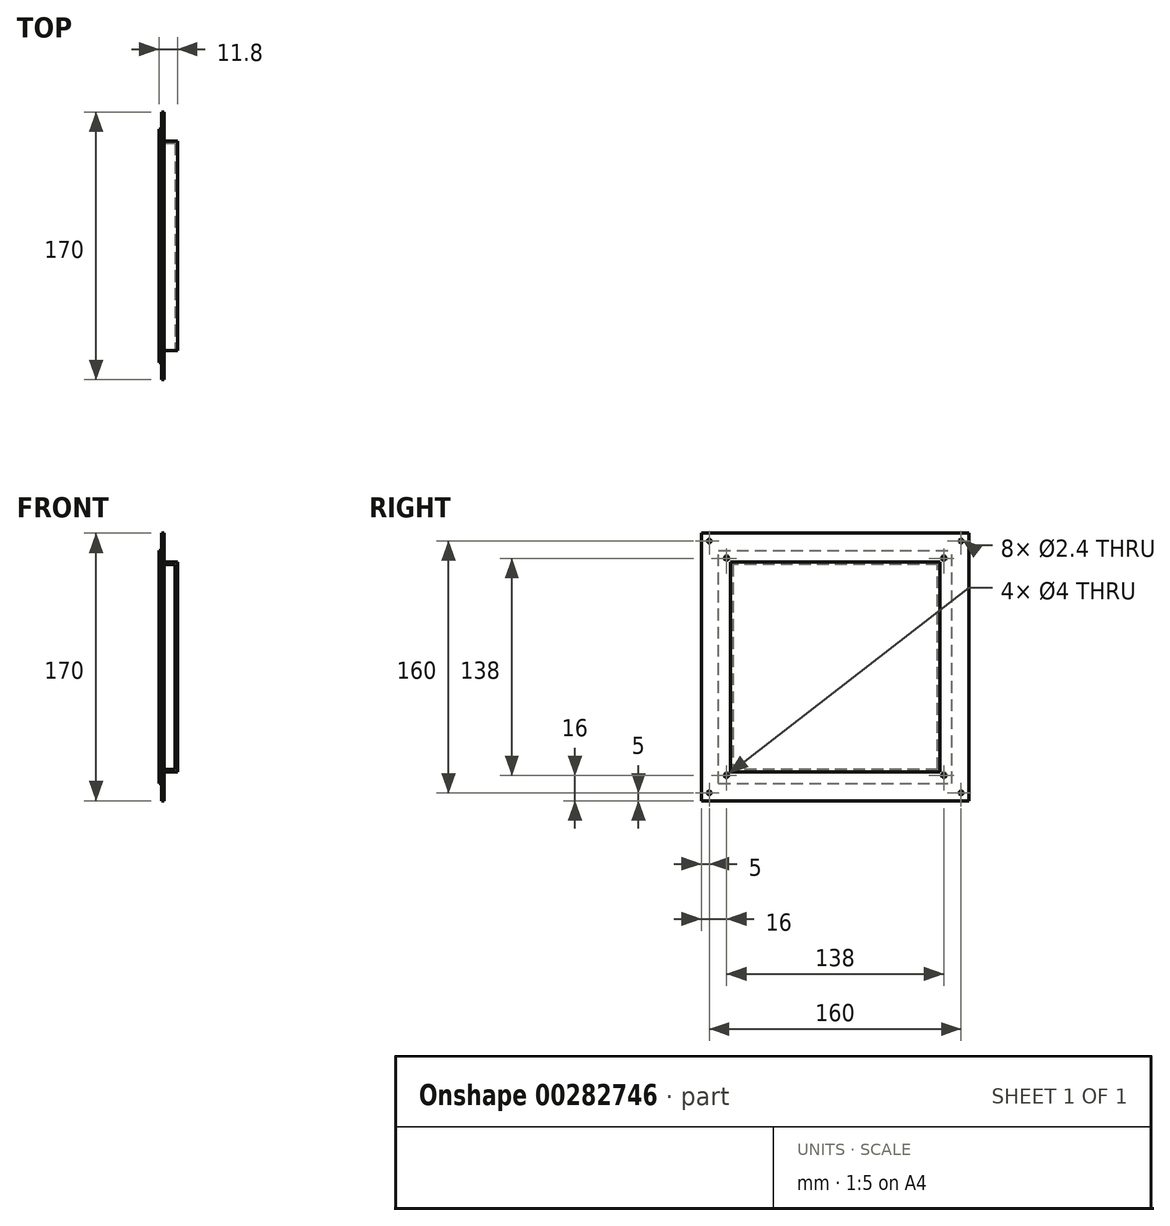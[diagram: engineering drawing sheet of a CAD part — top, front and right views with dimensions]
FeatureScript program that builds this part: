
annotation { "Feature Type Name" : "Feature", "Feature Type Description" : "" }
export const myFeature = defineFeature(function(context is Context, id is Id, definition is map)
    precondition{}
    {
        {
            var Q0;
            Q0=qCreatedBy(makeId("Right.planeOp"),FACE);
            var sketch = newSketch(context, id + "F0", { "sketchPlane" : qUnion([Q0])});
            skLineSegment(sketch, "E0.bottom", {"start": v(85, -85) * mm, "end": v(-85, -85) * mm});
            skLineSegment(sketch, "E0.top", {"start": v(85, 85) * mm, "end": v(-85, 85) * mm});
            skLineSegment(sketch, "E0.left", {"start": v(85, -85) * mm, "end": v(85, 85) * mm});
            skLineSegment(sketch, "E0.right", {"start": v(-85, -85) * mm, "end": v(-85, 85) * mm});
            skPoint(sketch, "E0.middle", {"position": v(0, 0) * mm});
            skLineSegment(sketch, "E1.bottom", {"start": v(66.6, -66.6) * mm, "end": v(-66.6, -66.6) * mm});
            skLineSegment(sketch, "E1.top", {"start": v(66.6, 66.6) * mm, "end": v(-66.6, 66.6) * mm});
            skLineSegment(sketch, "E1.left", {"start": v(66.6, -66.6) * mm, "end": v(66.6, 66.6) * mm});
            skLineSegment(sketch, "E1.right", {"start": v(-66.6, -66.6) * mm, "end": v(-66.6, 66.6) * mm});
            skPoint(sketch, "E2", {"position": v(-80, 80) * mm});
            skPoint(sketch, "E3", {"position": v(80, 80) * mm});
            skPoint(sketch, "E4", {"position": v(80, -80) * mm});
            skPoint(sketch, "E5", {"position": v(-80, -80) * mm});
            skPoint(sketch, "E6", {"position": v(-69, 69) * mm});
            skPoint(sketch, "E7", {"position": v(69, 69) * mm});
            skPoint(sketch, "E8", {"position": v(69, -69) * mm});
            skPoint(sketch, "E9", {"position": v(-69, -69) * mm});
            skSolve(sketch);
        }
        {
            var Q0;
            Q0=makeQuery(id+"F0.imprint","IMPRINT",FACE,{"disambiguationData":[TD([[makeQuery(id+"F0.imprint","IMPRINT",EDGE,{"derivedFrom":sQuery(id+"F0.wireOp",EDGE,"E0.bottom")}),-1.0]])]});
            extrude(context, id + "F1", {"entities" : qUnion([Q0]), "depth" : 1.6 * mm});
        }
        {
            var Q0;
            Q0=makeQuery(id+"F0.imprint","IMPRINT",FACE,{"disambiguationData":[TD([[makeQuery(id+"F0.imprint","IMPRINT",EDGE,{"derivedFrom":sQuery(id+"F0.wireOp",EDGE,"E1.bottom")}),-1.0]])]});
            extrude(context, id + "F2", {"entities" : qUnion([Q0]), "operationType" : NewBodyOperationType.ADD, "depth" : 10.2 * mm});
        }
        {
            var Q0;
            {var subQ0=sQuery(id+"F0.wireOp",EDGE,"E1.right");var subQ1=sQuery(id+"F0.wireOp",EDGE,"E1.left");var subQ2=sQuery(id+"F0.wireOp",EDGE,"E1.top");var subQ3=sQuery(id+"F0.wireOp",EDGE,"E1.bottom");Q0=makeQuery(id+"F2.boolean.opBoolean","MERGE",FACE,{"derivedFrom":[makeQuery(id+"F1.opExtrude","CAP_FACE",FACE,{"disambiguationData":[OSD([sQuery(id+"F0.wireOp",EDGE,"E0.bottom"),sQuery(id+"F0.wireOp",EDGE,"E0.top"),sQuery(id+"F0.wireOp",EDGE,"E0.left"),sQuery(id+"F0.wireOp",EDGE,"E0.right"),subQ3,subQ2,subQ1,subQ0])],"isStart":true}),makeQuery(id+"F2.opExtrude","CAP_FACE",FACE,{"disambiguationData":[OSD([subQ3,subQ2,subQ1,subQ0])],"isStart":true})]});}
            shell(context, id + "F3", {"entities" : qUnion([Q0]), "thickness" : 1.6 * mm});
        }
        {
            var Q0;
            Q0=makeQuery(id+"F2.opExtrude","SWEPT_FACE",FACE,{"disambiguationData":[OSD([sQuery(id+"F0.wireOp",EDGE,"E1.right")])]});
            var sketch = newSketch(context, id + "F4", { "sketchPlane" : qUnion([Q0])});
            skLineSegment(sketch, "E10.0", {"start": v(10.2, 66.6) * mm, "end": v(1.6, 66.6) * mm, "construction": true});
            skLineSegment(sketch, "E11.0", {"start": v(10.2, -66.6) * mm, "end": v(10.2, 66.6) * mm, "construction": true});
            skLineSegment(sketch, "E12.0", {"start": v(10.2, -66.6) * mm, "end": v(1.6, -66.6) * mm, "construction": true});
            skLineSegment(sketch, "E13.0", {"start": v(1.6, -85) * mm, "end": v(1.6, 85) * mm});
            skLineSegment(sketch, "E14.0", {"start": v(8.6, 65) * mm, "end": v(1.6, 65) * mm});
            skLineSegment(sketch, "E14.1", {"start": v(8.6, -65) * mm, "end": v(8.6, 65) * mm});
            skLineSegment(sketch, "E14.2", {"start": v(8.6, -65) * mm, "end": v(1.6, -65) * mm});
            skSolve(sketch);
        }
        {
            var Q0;
            {var subQ0=sQuery(id+"F4.wireOp",EDGE,"E14.0");Q0=makeQuery(id+"F4.imprint","IMPRINT",FACE,{"disambiguationData":[TD([[makeQuery(id+"F4.imprint","IMPRINT",EDGE,{"derivedFrom":subQ0}),1.0]])]});}
            extrude(context, id + "F5", {"entities" : qUnion([Q0]), "operationType" : NewBodyOperationType.REMOVE, "endBound" : BoundingType.UP_TO_NEXT, "oppositeDirection" : true, "depth" : 25 * mm});
        }
        {
            var Q0;
            Q0=sQuery(id+"F0.wireOp",VERTEX,"E3");
            var Q1;
            Q1=sQuery(id+"F0.wireOp",VERTEX,"E7");
            var Q2;
            Q2=sQuery(id+"F0.wireOp",VERTEX,"E8");
            var Q3;
            Q3=sQuery(id+"F0.wireOp",VERTEX,"E4");
            var Q4;
            Q4=sQuery(id+"F0.wireOp",VERTEX,"E9");
            var Q5;
            Q5=sQuery(id+"F0.wireOp",VERTEX,"E5");
            var Q6;
            Q6=sQuery(id+"F0.wireOp",VERTEX,"E2");
            var Q7;
            Q7=sQuery(id+"F0.wireOp",VERTEX,"E6");
            var Q8;
            Q8=makeQuery(id+"F1.opExtrude","SWEPT_BODY",BODY,{"disambiguationData":[OSD([sQuery(id+"F0.wireOp",EDGE,"E0.bottom"),sQuery(id+"F0.wireOp",EDGE,"E0.top"),sQuery(id+"F0.wireOp",EDGE,"E0.left"),sQuery(id+"F0.wireOp",EDGE,"E0.right"),sQuery(id+"F0.wireOp",EDGE,"E1.bottom"),sQuery(id+"F0.wireOp",EDGE,"E1.top"),sQuery(id+"F0.wireOp",EDGE,"E1.left"),sQuery(id+"F0.wireOp",EDGE,"E1.right")])]});
            hole(context, id + "F6", {"style" : HoleStyle.SIMPLE, "endStyle" : HoleEndStyle.THROUGH, "oppositeDirection" : true, "standardTappedOrClearance" : lookupTablePath({ "standard" : "ISO", "engagement" : "75%", "pitch" : "0.6 mm", "size" : "M3", "type" : "Tapped" }), "standardBlindInLast" : lookupTablePath({ "standard" : "ISO", "engagement" : "75%", "pitch" : "0.6 mm", "size" : "M3", "type" : "Tapped" }), "holeDiameter" : 2.4 * mm, "showTappedDepth" : true, "tappedDepth" : 12 * mm, "tapClearance" : 3, "startFromSketch" : true, "locations" : qUnion([Q0, Q1, Q2, Q3, Q4, Q5, Q6, Q7]), "scope" : qUnion([Q8])});
        }
        {
            var Q0;
            Q0=makeQuery(id+"F0.imprint","IMPRINT",FACE,{"disambiguationData":[TD([[makeQuery(id+"F0.imprint","IMPRINT",EDGE,{"derivedFrom":sQuery(id+"F0.wireOp",EDGE,"E0.bottom")}),-1.0]])]});
            var sketch = newSketch(context, id + "F7", { "sketchPlane" : qUnion([Q0])});
            skLineSegment(sketch, "E15.bottom", {"start": v(-74, -74) * mm, "end": v(74, -74) * mm});
            skLineSegment(sketch, "E15.top", {"start": v(-74, 74) * mm, "end": v(74, 74) * mm});
            skLineSegment(sketch, "E15.left", {"start": v(-74, -74) * mm, "end": v(-74, 74) * mm});
            skLineSegment(sketch, "E15.right", {"start": v(74, -74) * mm, "end": v(74, 74) * mm});
            skPoint(sketch, "E15.middle", {"position": v(0, 0) * mm});
            skPoint(sketch, "E16.0", {"position": v(-69, 69) * mm});
            skPoint(sketch, "E17.0", {"position": v(69, 69) * mm});
            skPoint(sketch, "E18.0", {"position": v(69, -69) * mm});
            skPoint(sketch, "E19.0", {"position": v(-69, -69) * mm});
            skCircle(sketch, "E20", {"center": v(69, 69) * mm, "radius": 2 * mm});
            skCircle(sketch, "E21", {"center": v(69, -69) * mm, "radius": 2 * mm});
            skCircle(sketch, "E22", {"center": v(-69, -69) * mm, "radius": 2 * mm});
            skCircle(sketch, "E23", {"center": v(-69, 69) * mm, "radius": 2 * mm});
            skSolve(sketch);
        }
        {
            var Q0;
            Q0 = qSketchRegion(id + "F7", true);
            extrude(context, id + "F8", {"entities" : qUnion([Q0]), "oppositeDirection" : true, "depth" : 1.6 * mm});
        }
    });
